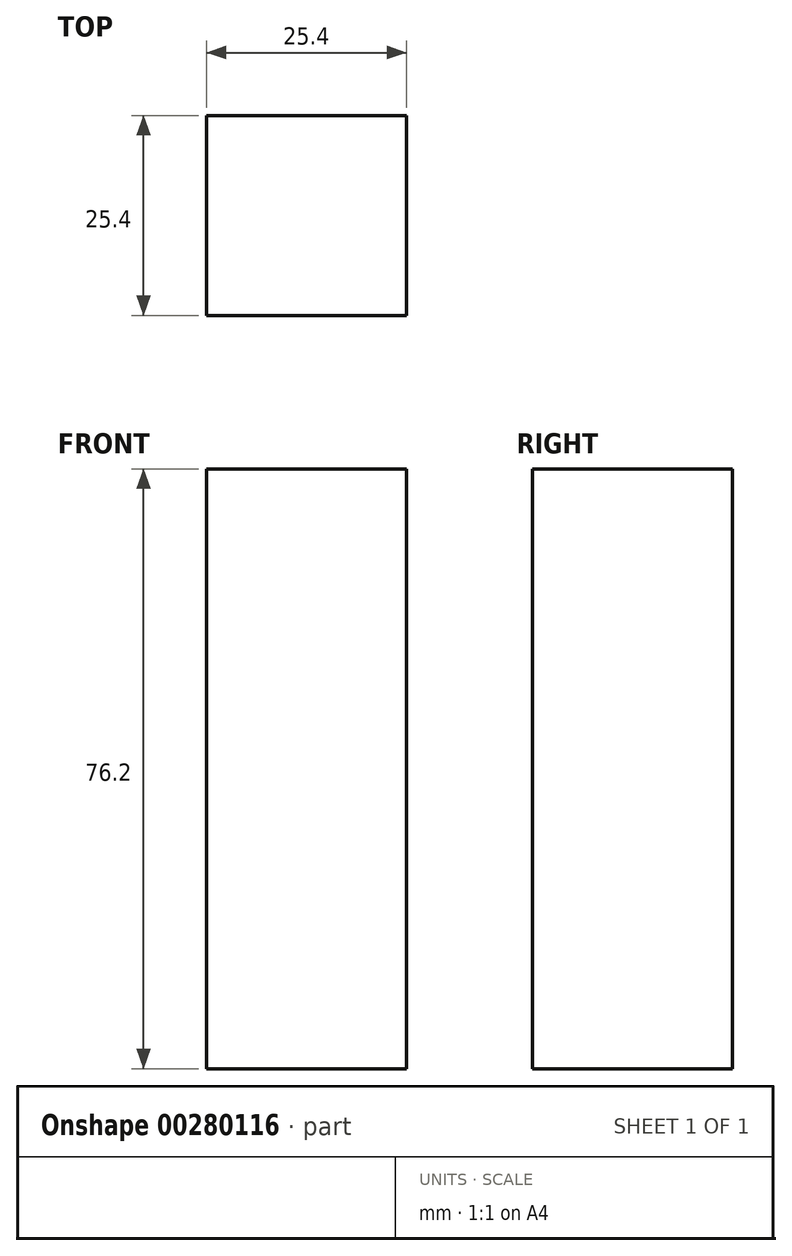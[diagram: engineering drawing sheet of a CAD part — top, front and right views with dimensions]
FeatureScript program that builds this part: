
annotation { "Feature Type Name" : "Feature", "Feature Type Description" : "" }
export const myFeature = defineFeature(function(context is Context, id is Id, definition is map)
    precondition{}
    {
        {
            var Q0;
            Q0=qCreatedBy(makeId("Front.planeOp"),FACE);
            var sketch = newSketch(context, id + "F0", { "sketchPlane" : qUnion([Q0])});
            skLineSegment(sketch, "E0.bottom", {"start": v(0, 0) * mm, "end": v(-25.4, 0) * mm});
            skLineSegment(sketch, "E0.top", {"start": v(0, 76.2) * mm, "end": v(-25.4, 76.2) * mm});
            skLineSegment(sketch, "E0.left", {"start": v(0, 0) * mm, "end": v(0, 76.2) * mm});
            skLineSegment(sketch, "E0.right", {"start": v(-25.4, 0) * mm, "end": v(-25.4, 76.2) * mm});
            skSolve(sketch);
        }
        {
            var Q0;
            Q0 = qSketchRegion(id + "F0", true);
            extrude(context, id + "F1", {"entities" : qUnion([Q0]), "depth" : 25.4 * mm});
        }
    });
